# Revit family: Arper_Aava-02_chair_4legs_upholstery_7618
name_source: partatom
category: Furniture
units: mm (PartAtom-declared; Revit-internal decimal feet)

## family parameters
Always vertical = Yes
Cut with Voids When Loaded = No
OmniClass Number = 23.40.20.00
OmniClass Title = General Furniture and Specialties
Room Calculation Point = No
Shared = No
Work Plane-Based = No

## types (1)
- Arper_Aava-02_chair_4legs_upholstery_7618
    Default Elevation = 0 mm  [stored 0 ft]
    Description = Chair on a 4-leg base in chromed or powder-coated steel. Shell in 
polypropylene made with post-consumer recycled materials, mixed 
with virgin material, with upholstery in fabric, leather, coated fabric or 
customer’s own material. The upholstery can be separated and 
replaced by technical personnel, since it has been applied without 
the use of glue. Glides are also available, with felt insert for wood 
floors.
    Manufacturer = ARPER s.p.a.
    Model = Aava 02
    URL = http://www.arper.com

note: [stored X ft] marks values corroborated as IEEE doubles in the binary element streams (Revit-internal decimal feet)
